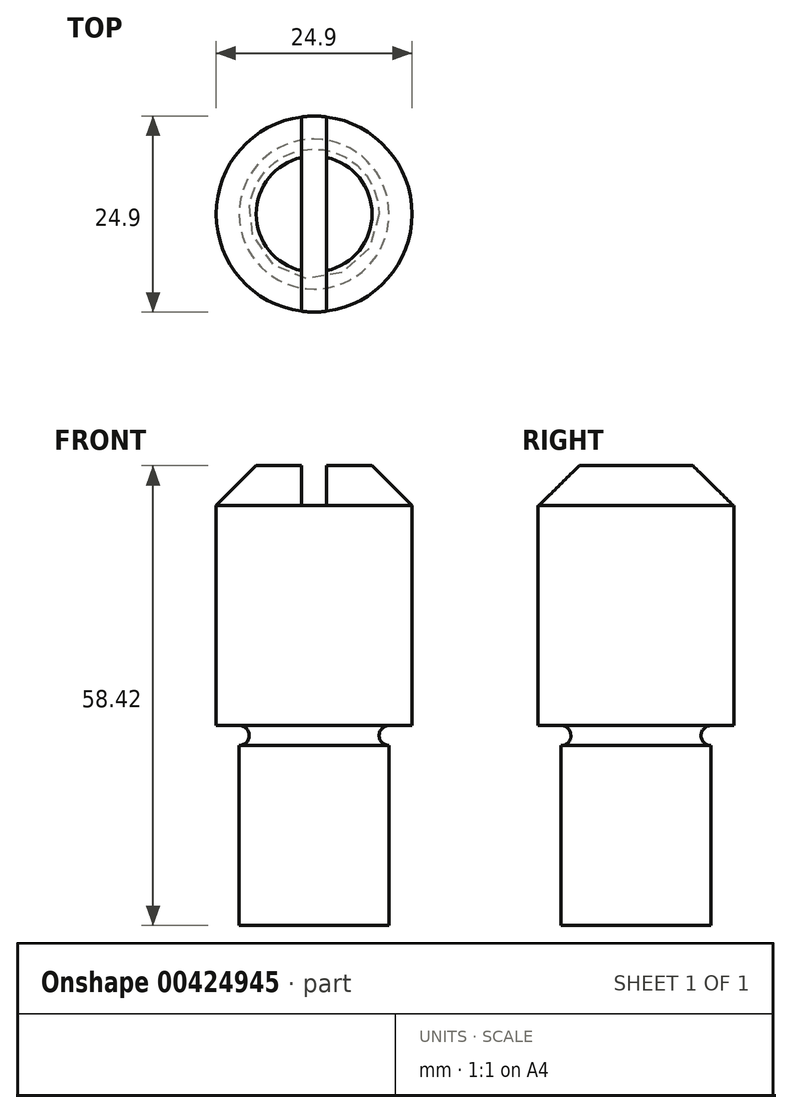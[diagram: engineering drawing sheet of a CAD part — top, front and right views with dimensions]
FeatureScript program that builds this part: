
annotation { "Feature Type Name" : "Feature", "Feature Type Description" : "" }
export const myFeature = defineFeature(function(context is Context, id is Id, definition is map)
    precondition{}
    {
        {
            var Q0;
            Q0=qCreatedBy(makeId("Front.planeOp"),FACE);
            var sketch = newSketch(context, id + "F0", { "sketchPlane" : qUnion([Q0])});
            skLineSegment(sketch, "E0", {"start": v(0, 0) * mm, "end": v(0, -58.42) * mm});
            skLineSegment(sketch, "E1", {"start": v(0, -58.42) * mm, "end": v(-9.52, -58.42) * mm});
            skLineSegment(sketch, "E2", {"start": v(-9.53, -58.42) * mm, "end": v(-9.53, -35.56) * mm});
            skLineSegment(sketch, "E3", {"start": v(-9.52, -33.02) * mm, "end": v(-12.45, -33.02) * mm});
            skLineSegment(sketch, "E4", {"start": v(-12.45, -33.02) * mm, "end": v(-12.45, -5.08) * mm});
            skLineSegment(sketch, "E5", {"start": v(-12.45, -5.08) * mm, "end": v(-7.37, 0) * mm});
            skLineSegment(sketch, "E6", {"start": v(-7.37, 0) * mm, "end": v(0, 0) * mm});
            skArc(sketch, "E7", {"start": v(-9.53, -35.56) * mm, "mid": v(-8.25, -34.29) * mm, "end": v(-9.52, -33.02) * mm});
            skSolve(sketch);
        }
        {
            var Q0;
            Q0=makeQuery(id+"F0.imprint","IMPRINT",FACE,{"disambiguationData":[TD([[makeQuery(id+"F0.imprint","IMPRINT",EDGE,{"derivedFrom":sQuery(id+"F0.wireOp",EDGE,"E0")}),-1.0]])]});
            var Q1;
            Q1=sQuery(id+"F0.wireOp",EDGE,"E0");
            revolve(context, id + "F1", {"entities" : qUnion([Q0]), "axis" : qUnion([Q1]), "revolveType" : RevolveType.FULL});
        }
        {
            var Q0;
            Q0=qCreatedBy(makeId("Front.planeOp"),FACE);
            var sketch = newSketch(context, id + "F2", { "sketchPlane" : qUnion([Q0])});
            skLineSegment(sketch, "E8", {"start": v(0, -70.34) * mm, "end": v(0, 0) * mm, "construction": true});
            skLineSegment(sketch, "E9.bottom", {"start": v(1.59, -5.08) * mm, "end": v(-1.59, -5.08) * mm});
            skLineSegment(sketch, "E9.top", {"start": v(1.59, 5.08) * mm, "end": v(-1.59, 5.08) * mm});
            skLineSegment(sketch, "E9.left", {"start": v(1.59, -5.08) * mm, "end": v(1.59, 5.08) * mm});
            skLineSegment(sketch, "E9.right", {"start": v(-1.59, -5.08) * mm, "end": v(-1.59, 5.08) * mm});
            skPoint(sketch, "E9.middle", {"position": v(0, 0) * mm});
            skSolve(sketch);
        }
        {
            var Q0;
            Q0 = qSketchRegion(id + "F2", true);
            extrude(context, id + "F3", {"entities" : qUnion([Q0]), "operationType" : NewBodyOperationType.REMOVE, "oppositeDirection" : true, "depth" : 25.4 * mm, "symmetric" : true});
        }
    });
